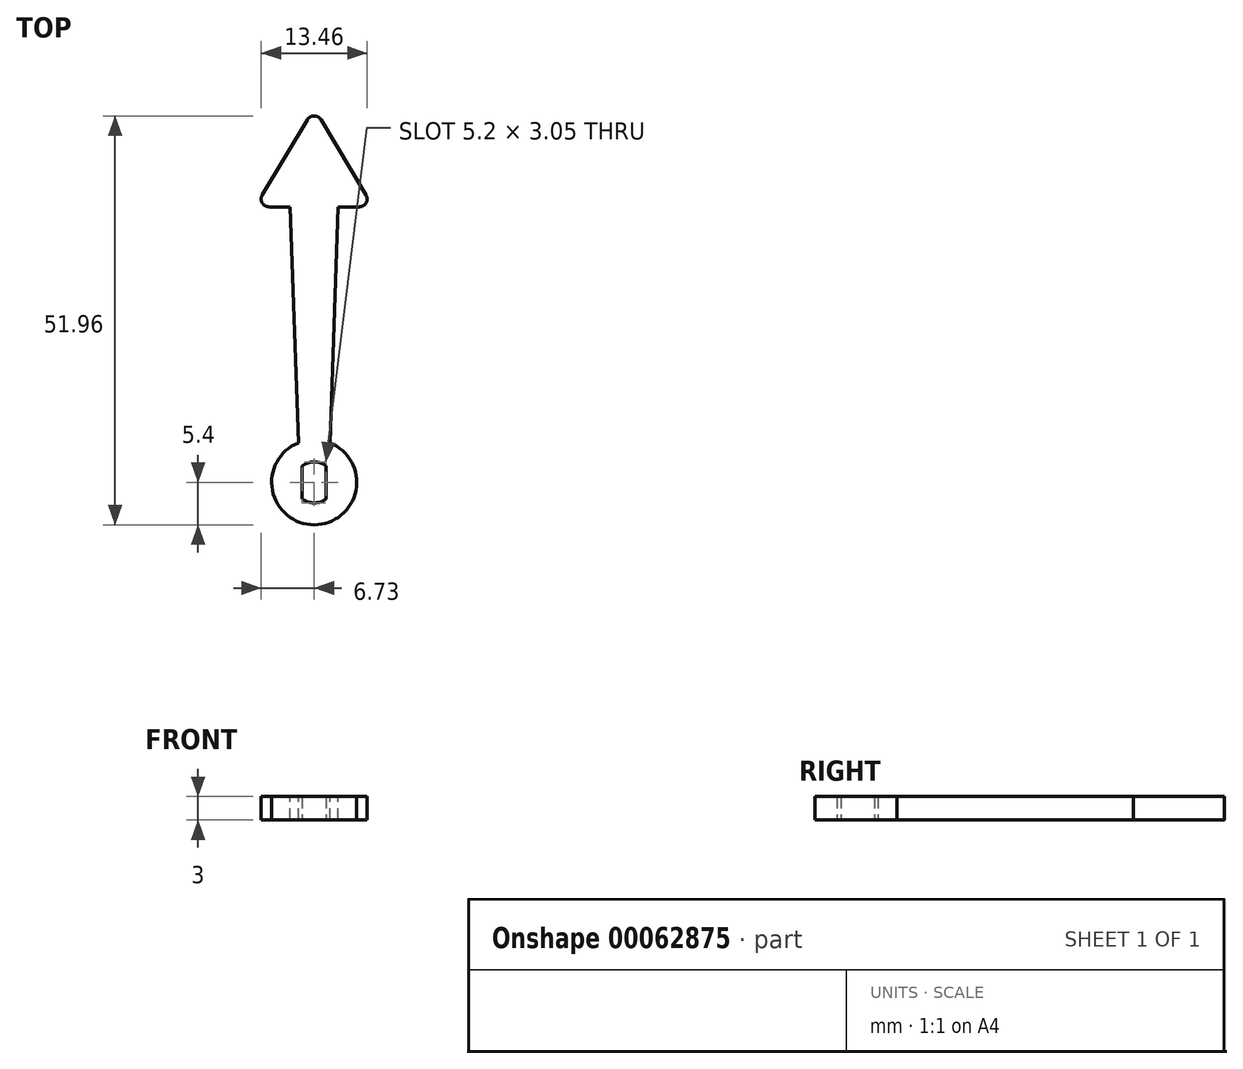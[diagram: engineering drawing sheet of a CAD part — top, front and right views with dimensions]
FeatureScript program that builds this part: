
annotation { "Feature Type Name" : "Feature", "Feature Type Description" : "" }
export const myFeature = defineFeature(function(context is Context, id is Id, definition is map)
    precondition{}
    {
        {
            var Q0;
            Q0=qCreatedBy(makeId("Top.planeOp"),FACE);
            var sketch = newSketch(context, id + "F0", { "sketchPlane" : qUnion([Q0])});
            skCircle(sketch, "E0", {"center": v(0, 0) * mm, "radius": 5.4 * mm});
            skCircle(sketch, "E1", {"center": v(0, 0) * mm, "radius": 2.6 * mm});
            skLineSegment(sketch, "E2", {"start": v(-1.53, 2.1) * mm, "end": v(-1.53, -2.1) * mm});
            skLineSegment(sketch, "E3", {"start": v(1.52, 2.1) * mm, "end": v(1.52, -2.1) * mm});
            skSolve(sketch);
        }
        {
            var Q0;
            Q0 = qSketchRegion(id + "F0", true);
            var Q1;
            {var subQ0=sQuery(id+"F0.wireOp",EDGE,"E3");Q1=makeQuery(id+"F0.imprint","IMPRINT",FACE,{"disambiguationData":[TD([[makeQuery(id+"F0.imprint","IMPRINT",EDGE,{"derivedFrom":subQ0}),1.0]])]});}
            var Q2;
            {var subQ0=sQuery(id+"F0.wireOp",EDGE,"E2");Q2=makeQuery(id+"F0.imprint","IMPRINT",FACE,{"disambiguationData":[TD([[makeQuery(id+"F0.imprint","IMPRINT",EDGE,{"derivedFrom":subQ0}),-1.0]])]});}
            extrude(context, id + "F1", {"entities" : qUnion([Q0, Q1, Q2]), "endBound" : BoundingType.SYMMETRIC, "depth" : 3 * mm});
        }
        {
            var Q0;
            Q0=makeQuery(id+"F1.opExtrude","CAP_FACE",FACE,{"disambiguationData":[OSD([sQuery(id+"F0.wireOp",EDGE,"E0"),sQuery(id+"F0.wireOp",EDGE,"E1"),sQuery(id+"F0.wireOp",EDGE,"E2"),sQuery(id+"F0.wireOp",EDGE,"E3")])],"isStart":false});
            var sketch = newSketch(context, id + "F2", { "sketchPlane" : qUnion([Q0])});
            skLineSegment(sketch, "E4", {"start": v(0, 0) * mm, "end": v(0, 35) * mm, "construction": true});
            skLineSegment(sketch, "E5", {"start": v(0, 35) * mm, "end": v(3.05, 35) * mm});
            skLineSegment(sketch, "E6", {"start": v(0, 5.02) * mm, "end": v(2, 5.02) * mm});
            skLineSegment(sketch, "E7", {"start": v(3.05, 35) * mm, "end": v(2, 5.02) * mm});
            skLineSegment(sketch, "E8.MirrorCS", {"start": v(0, 35) * mm, "end": v(-3.05, 35) * mm});
            skLineSegment(sketch, "E9.MirrorCS", {"start": v(-3.05, 35) * mm, "end": v(-2, 5.02) * mm});
            skLineSegment(sketch, "E10.MirrorCS", {"start": v(0, 5.02) * mm, "end": v(-2, 5.02) * mm});
            skSolve(sketch);
        }
        {
            var Q0;
            Q0 = qSketchRegion(id + "F2", true);
            var Q1;
            Q1=makeQuery(id+"F1.opExtrude","CAP_FACE",FACE,{"disambiguationData":[OSD([sQuery(id+"F0.wireOp",EDGE,"E0"),sQuery(id+"F0.wireOp",EDGE,"E1"),sQuery(id+"F0.wireOp",EDGE,"E2"),sQuery(id+"F0.wireOp",EDGE,"E3")])],"isStart":true});
            extrude(context, id + "F3", {"entities" : qUnion([Q0]), "operationType" : NewBodyOperationType.ADD, "endBound" : BoundingType.UP_TO_SURFACE, "oppositeDirection" : true, "endBoundEntityFace" : qUnion([Q1]), "depth" : 25 * mm});
        }
        {
            var Q0;
            Q0=makeQuery(id+"F3.boolean.opBoolean","MERGE",FACE,{"derivedFrom":[makeQuery(id+"F1.opExtrude","CAP_FACE",FACE,{"disambiguationData":[OSD([sQuery(id+"F0.wireOp",EDGE,"E0"),sQuery(id+"F0.wireOp",EDGE,"E1"),sQuery(id+"F0.wireOp",EDGE,"E2"),sQuery(id+"F0.wireOp",EDGE,"E3")])],"isStart":false}),makeQuery(id+"F3.opExtrude","CAP_FACE",FACE,{"disambiguationData":[OSD([sQuery(id+"F2.wireOp",EDGE,"E5"),sQuery(id+"F2.wireOp",EDGE,"E6"),sQuery(id+"F2.wireOp",EDGE,"E7"),sQuery(id+"F2.wireOp",EDGE,"E8.MirrorCS"),sQuery(id+"F2.wireOp",EDGE,"E9.MirrorCS"),sQuery(id+"F2.wireOp",EDGE,"E10.MirrorCS")])],"isStart":true})]});
            var sketch = newSketch(context, id + "F4", { "sketchPlane" : qUnion([Q0])});
            skLineSegment(sketch, "E11", {"start": v(0, 35) * mm, "end": v(0, 47.5) * mm, "construction": true});
            skPoint(sketch, "E11.endSnap0", {"position": v(0, 35) * mm});
            skLineSegment(sketch, "E12", {"start": v(-7.5, 35) * mm, "end": v(7.5, 35) * mm});
            skLineSegment(sketch, "E13", {"start": v(0, 47.5) * mm, "end": v(7.5, 35) * mm});
            skLineSegment(sketch, "E14", {"start": v(0, 47.5) * mm, "end": v(-7.5, 35) * mm});
            skSolve(sketch);
        }
        {
            var Q0;
            Q0 = qSketchRegion(id + "F4", true);
            var Q1;
            Q1=makeQuery(id+"F3.boolean.opBoolean","MERGE",FACE,{"derivedFrom":[makeQuery(id+"F1.opExtrude","CAP_FACE",FACE,{"disambiguationData":[OSD([sQuery(id+"F0.wireOp",EDGE,"E0"),sQuery(id+"F0.wireOp",EDGE,"E1"),sQuery(id+"F0.wireOp",EDGE,"E2"),sQuery(id+"F0.wireOp",EDGE,"E3")])],"isStart":true}),makeQuery(id+"F3.opExtrude","CAP_FACE",FACE,{"disambiguationData":[OSD([sQuery(id+"F2.wireOp",EDGE,"E5"),sQuery(id+"F2.wireOp",EDGE,"E6"),sQuery(id+"F2.wireOp",EDGE,"E7"),sQuery(id+"F2.wireOp",EDGE,"E8.MirrorCS"),sQuery(id+"F2.wireOp",EDGE,"E9.MirrorCS"),sQuery(id+"F2.wireOp",EDGE,"E10.MirrorCS")])],"isStart":false})]});
            extrude(context, id + "F5", {"entities" : qUnion([Q0]), "operationType" : NewBodyOperationType.ADD, "endBound" : BoundingType.UP_TO_SURFACE, "oppositeDirection" : true, "endBoundEntityFace" : qUnion([Q1]), "depth" : 25 * mm});
        }
        {
            var Q0;
            Q0=makeQuery(id+"F5.opExtrude","SWEPT_EDGE",EDGE,{"disambiguationData":[OSD([sQuery(id+"F4.wireOp",EDGE,"E12"),sQuery(id+"F4.wireOp",EDGE,"E13")])]});
            var Q1;
            Q1=makeQuery(id+"F5.opExtrude","SWEPT_EDGE",EDGE,{"disambiguationData":[OSD([sQuery(id+"F4.wireOp",EDGE,"E12"),sQuery(id+"F4.wireOp",EDGE,"E14")])]});
            var Q2;
            Q2=makeQuery(id+"F5.opExtrude","SWEPT_EDGE",EDGE,{"disambiguationData":[OSD([sQuery(id+"F4.wireOp",EDGE,"E13"),sQuery(id+"F4.wireOp",EDGE,"E14")])]});
            fillet(context, id + "F6", {"entities" : qUnion([Q0, Q1, Q2]), "radius" : 1 * mm, "tangentPropagation" : true, "allowEdgeOverflow" : false});
        }
    });
